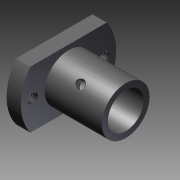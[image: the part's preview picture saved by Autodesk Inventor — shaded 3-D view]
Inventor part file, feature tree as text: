
AUTODESK INVENTOR PART (.ipt)
format: ipt  version: 2016 (Build 200138000, 138)  size: 165,376 bytes
history: native  units: mm
features: other x14, sketch x6, revolve x5, thread x4, extrude x1
ambient origin geometry x8: Origin, YZ Plane, XZ Plane, XY Plane, X Axis, Y Axis, Z Axis, Center Point
bodies: Solid1 (feature_tree)
feature tree (30):
  revolve  "Revolution1"  Angle=360.0deg
  revolve  "Revolution2"  Angle=360.0deg
  thread  "Thread1"  [1 undecoded]
  revolve  "Revolution3"  Angle=360.0deg
  thread  "Thread2"  [1 undecoded]
  extrude  "Extrusion1"  Depth=5.242mm TaperAngle=0.0deg
  revolve  "Revolution4"  [1 undecoded]
  thread  "Thread3"  [1 undecoded]
  revolve  "Revolution5"  [1 undecoded]
  thread  "Thread4"  [1 undecoded]
  other  "to_screw1_XY"
  other  "to_screw1_YZ"
  other  "to_screw1_ZX"
  other  "to_screw1_X"
  other  "to_screw1_Y"
  other  "to_screw1_Z"
  other  "to_screw1_Center"
  other  "to_screw2_XY"
  other  "to_screw2_YZ"
  other  "to_screw2_ZX"
  other  "to_screw2_X"
  other  "to_screw2_Y"
  other  "to_screw2_Z"
  other  "to_screw2_Center"
  sketch  "Sketch_1"  dims[d0=360.0deg d1=360.0deg]
  sketch  "Sketch_3"  dims[d7=30.0mm d8=0.0mm d9=360.0deg d10=5.242mm d11=0.0mm]
  sketch  "Sketch_2"  dims[d2=2.39258mm d3=0.0mm d4=360.0deg d5=2.39258mm d6=0.0mm]
  sketch  "Sketch_4"  dims[d12=360.0deg d13=5.242mm d14=0.0mm]
  sketch  "Sketch_12"
  sketch  "Sketch_14"
note: 6 required parameter values undecoded (feature->parameter linkage not recoverable at this tier; creation-order binding heuristic only, values carry confidence <= 0.55)
